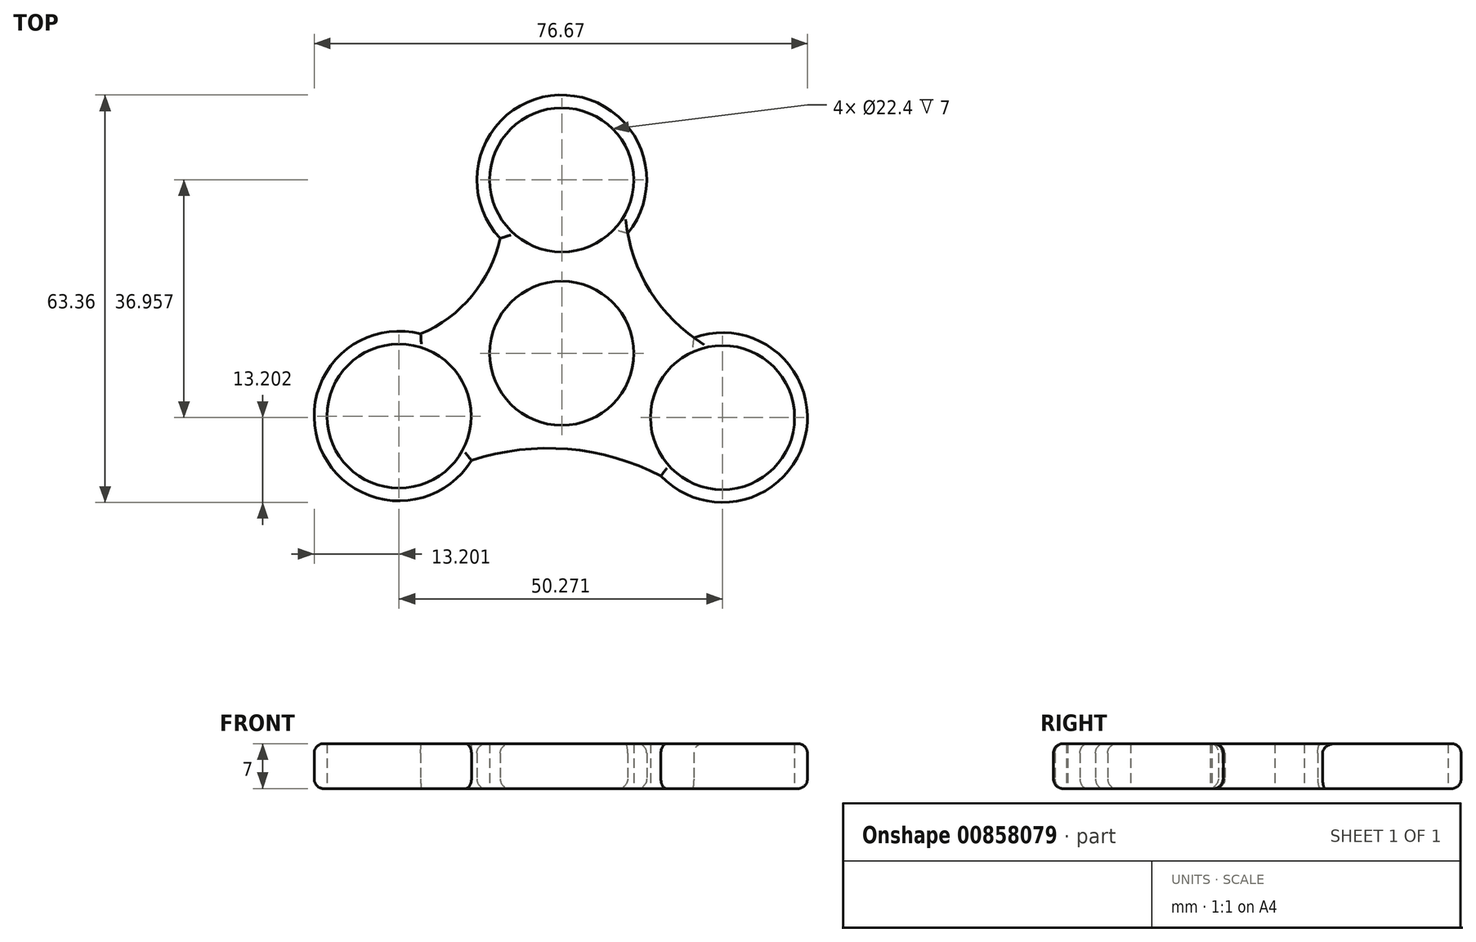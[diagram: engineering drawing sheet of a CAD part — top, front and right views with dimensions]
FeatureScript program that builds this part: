
annotation { "Feature Type Name" : "Feature", "Feature Type Description" : "" }
export const myFeature = defineFeature(function(context is Context, id is Id, definition is map)
    precondition{}
    {
        {
            var Q0;
            Q0=qCreatedBy(makeId("Top.planeOp"),FACE);
            var sketch = newSketch(context, id + "F0", { "sketchPlane" : qUnion([Q0])});
            skCircle(sketch, "E0", {"center": v(0, 26.97) * mm, "radius": 11.2 * mm});
            skArc(sketch, "E1", {"start": v(10.25, 18.65) * mm, "mid": v(-0.5, 40.16) * mm, "end": v(-9.58, 17.88) * mm});
            skCircle(sketch, "E2", {"center": v(-25.29, -9.76) * mm, "radius": 11.2 * mm});
            skArc(sketch, "E3", {"start": v(-21.93, 3) * mm, "mid": v(-37.54, -14.68) * mm, "end": v(-14.03, -16.66) * mm});
            skCircle(sketch, "E4", {"center": v(24.98, -9.99) * mm, "radius": 11.2 * mm});
            skArc(sketch, "E5", {"start": v(15.4, -19.07) * mm, "mid": v(37.83, -13.04) * mm, "end": v(20.5, 2.43) * mm});
            skArc(sketch, "E6", {"start": v(-21.93, 3) * mm, "mid": v(-13.95, 8.95) * mm, "end": v(-9.58, 17.88) * mm});
            skArc(sketch, "E7", {"start": v(10.25, 18.65) * mm, "mid": v(13.81, 9.55) * mm, "end": v(20.5, 2.43) * mm});
            skArc(sketch, "E8", {"start": v(15.4, -19.07) * mm, "mid": v(0.93, -14.9) * mm, "end": v(-14.03, -16.66) * mm});
            skCircle(sketch, "E9", {"center": v(0, 0) * mm, "radius": 11.2 * mm});
            skSolve(sketch);
        }
        {
            var Q0;
            Q0=makeQuery(id+"F0.imprint","IMPRINT",FACE,{"disambiguationData":[TD([[makeQuery(id+"F0.imprint","IMPRINT",EDGE,{"derivedFrom":sQuery(id+"F0.wireOp",EDGE,"E0")}),-1.0]])]});
            extrude(context, id + "F1", {"entities" : qUnion([Q0]), "depth" : 7 * mm, "offsetDistance" : 25 * mm});
        }
        {
            var Q0;
            Q0=makeQuery(id+"F1.opExtrude","CAP_EDGE",EDGE,{"disambiguationData":[OSD([sQuery(id+"F0.wireOp",EDGE,"E8")])],"isStart":false});
            var Q1;
            Q1=makeQuery(id+"F1.opExtrude","CAP_EDGE",EDGE,{"disambiguationData":[OSD([sQuery(id+"F0.wireOp",EDGE,"E3")])],"isStart":false});
            var Q2;
            Q2=makeQuery(id+"F1.opExtrude","CAP_EDGE",EDGE,{"disambiguationData":[OSD([sQuery(id+"F0.wireOp",EDGE,"E6")])],"isStart":false});
            var Q3;
            Q3=makeQuery(id+"F1.opExtrude","CAP_EDGE",EDGE,{"disambiguationData":[OSD([sQuery(id+"F0.wireOp",EDGE,"E1")])],"isStart":false});
            var Q4;
            Q4=makeQuery(id+"F1.opExtrude","CAP_EDGE",EDGE,{"disambiguationData":[OSD([sQuery(id+"F0.wireOp",EDGE,"E5")])],"isStart":false});
            var Q5;
            Q5=makeQuery(id+"F1.opExtrude","CAP_EDGE",EDGE,{"disambiguationData":[OSD([sQuery(id+"F0.wireOp",EDGE,"E8")])],"isStart":true});
            fillet(context, id + "F2", {"entities" : qUnion([Q0, Q1, Q2, Q3, Q4, Q5]), "radius" : 1.5 * mm, "tangentPropagation" : true, "allowEdgeOverflow" : false});
        }
        {
            var Q0;
            Q0=makeQuery(id+"F1.opExtrude","CAP_EDGE",EDGE,{"disambiguationData":[OSD([sQuery(id+"F0.wireOp",EDGE,"E3")])],"isStart":true});
            var Q1;
            Q1=makeQuery(id+"F1.opExtrude","CAP_EDGE",EDGE,{"disambiguationData":[OSD([sQuery(id+"F0.wireOp",EDGE,"E6")])],"isStart":true});
            var Q2;
            Q2=makeQuery(id+"F1.opExtrude","CAP_EDGE",EDGE,{"disambiguationData":[OSD([sQuery(id+"F0.wireOp",EDGE,"E1")])],"isStart":true});
            var Q3;
            Q3=makeQuery(id+"F1.opExtrude","CAP_EDGE",EDGE,{"disambiguationData":[OSD([sQuery(id+"F0.wireOp",EDGE,"E7")])],"isStart":true});
            var Q4;
            Q4=makeQuery(id+"F1.opExtrude","CAP_EDGE",EDGE,{"disambiguationData":[OSD([sQuery(id+"F0.wireOp",EDGE,"E5")])],"isStart":true});
            fillet(context, id + "F3", {"entities" : qUnion([Q0, Q1, Q2, Q3, Q4]), "radius" : 1.5 * mm, "tangentPropagation" : true, "allowEdgeOverflow" : false});
        }
    });
